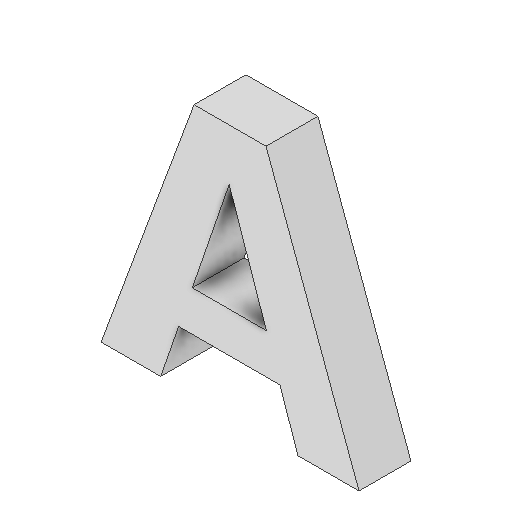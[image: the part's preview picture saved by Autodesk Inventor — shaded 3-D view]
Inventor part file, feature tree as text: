
AUTODESK INVENTOR PART (.ipt)
format: ipt  version: 2025 (Build 290162000, 162)  size: 126,976 bytes
history: native  units: mm
features: reference x11, extrude x2, sketch x2, other x2
ambient origin geometry x8: Origin, YZ Plane, XZ Plane, XY Plane, X Axis, Y Axis, Z Axis, Center Point
bodies: Solid1 (feature_tree)
feature tree (17):
  extrude  "Extrusion1"  Depth=1.4mm TaperAngle=0.0deg
  extrude  "Extrusion2"  Depth=0.1mm
  sketch  "Sketch1"  dims[d0=40.0mm d1=1.4mm d2=0.0mm]
  sketch  "Sketch3"  dims[d5=0.1mm d6=0.1mm d7=10.0mm d8=0.0mm]
  reference  "Reference12"
  reference  "Reference13"
  reference  "Reference14"
  reference  "Reference15"
  reference  "Reference16"
  reference  "Reference17"
  reference  "Reference18"
  reference  "Reference19"
  reference  "Reference20"
  reference  "Reference21"
  reference  "Reference22"
  other  "USB_C_PD_PPS_sink_with_enclosure.iam"
  other  "display_cover_2:1"
